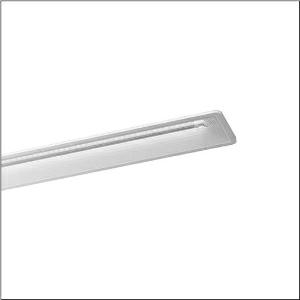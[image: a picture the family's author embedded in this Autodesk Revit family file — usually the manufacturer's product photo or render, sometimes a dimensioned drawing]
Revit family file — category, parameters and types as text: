
# Revit family: taris_r__21_5mt117703wd_45ff
name_source: partatom
category: Lighting Fixtures
units: mm (PartAtom-declared; Revit-internal decimal feet)

## family parameters
Cut with Voids When Loaded = No
Host = Face
Light Source = No
Part Type = Normal
Room Calculation Point = No
Round Connector Dimension = Use Diameter
Shared = No

## types (1)
- Taris® 21 (1 x LED, 5700 lm, 37 W, 3000K)
    Apparent Load = 37 VA
    CIE Flux Codes = 73 96 99 100 100
    Color Rendering = 80
    Color Temperature = 3000K
    Default Elevation = 1800 mm
    Description = Taris® 21, office luminaire, primary anti-glare with micro louvre, primary optical cover: axial lens, of PMMA, structured, CAT 2 (L<= 1500cd/m²), light emission: direct distribution, primary light characteristic: symmetric, installation type: recessed, LED, rated luminous flux: 5.700lm, luminous efficacy: 154lm/W, light colour: 830, colour temperature: 3000K, control gear: ECG, with terminal, 5-pole, mains connection: 230V, AC, 50Hz, rated input power: 37W, housing, luminaire housing, of plastic, pure white, length: 1.530mm, width: 150mm, height: 76mm, recess depth: 106mm, protection rating (complete): IP20, insulation class (complete): insulation class I (protective earthing), certification: CE, ENEC, VDE, protection symbol: F, impact resistance: IK02, permissible operating ambient temperature: 0..+35°C, standard: EN 50419, packaging unit: 1 piece
    Height = 0 mm  [stored 0 ft]
    Lamp = 1 x LED
    Lamp Light Flux = 5700 lm
    Lamp Power = 37 W
    Lamp count = 1
    Length = 1524 mm  [stored 5 ft]
    Luminous efficacy = 154 lm/W
    Manufacturer = Siteco
    ModVariant = No
    Model = 5MT117703WD
    Mounting Place = Ceiling
    Mounting Type = Recessed
    Number of Poles = 1
    OnlyDefault = Yes
    Power Factor = 1
    Product Name = Taris® 21
    Product group = office luminaire | ceiling recessed
    ProductGroupID = 401
    Protection Class = Protection class I
    Protection Degree = IP 20
    RLX_Detail_Level = 1
    RLX_Emergency_Light_Flux = 0 lm
    RLX_Emergency_Type = 0
    RLX_Emergency_Type_DB = No
    RlxData = <blob elided: 26589 chars, md5=f197acfd>
    Socket = socket
    Standby Power = 0 W
    System Light Flux = 5700 lm
    System Power = 37 W
    Type Comments = Product without accessories
    Type Image = l_1004723.jpg
    URL = http://relux.com
    VarID = ---
    Voltage = 0 V
    Weight = 0.00 kg
    Width = 144 mm

note: [stored X ft] marks values corroborated as IEEE doubles in the binary element streams (Revit-internal decimal feet)

## geometry (parser evidence)
native form markers: Blend x4, Sweep x10
no freeform markers — native parametric forms only
